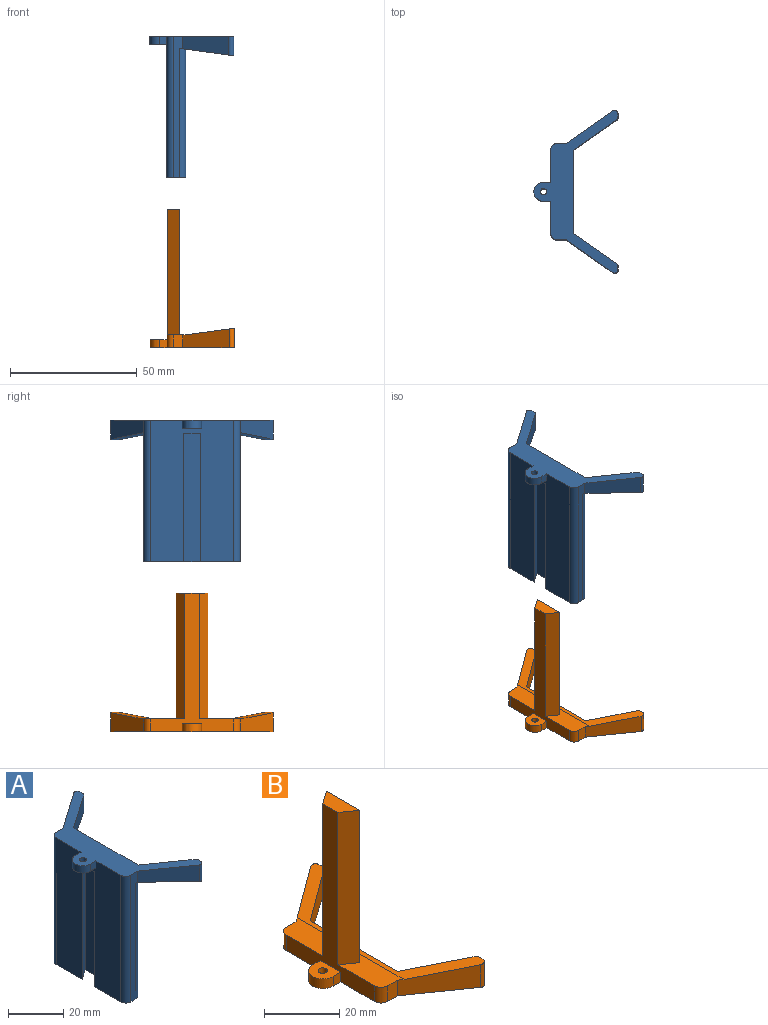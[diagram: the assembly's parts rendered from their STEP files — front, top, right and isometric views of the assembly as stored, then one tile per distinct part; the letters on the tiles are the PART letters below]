
ASSEMBLY  parts=2 mates=1
PART A: 31 faces, bbox 33.1x64.2x55.9 mm
  f0: plane 7.62x1.43mm, normal (1,0,0), area 10.9mm2, adj f4,f6,f28,f29
  f1: plane 55.88x33.02mm, normal (-1,0,0), area 1498.6mm2, adj f2,f6,f9,f11,f12,f13,f15,f17
  f2: plane 38.1x7.62mm, normal (0,0,-1), area 234.3mm2, adj f1,f3,f7,f8,f9,f10,f11,f18
  f3: plane 50.8x33.02mm, normal (1,0,0), area 1677.4mm2, adj f2,f4,f18,f20
  f4: plane 64.23x21.42mm, normal (-0.13,0,-0.99), area 215.4mm2, adj f0,f3,f5,f7,f8,f18,f20,f22
  f5: plane 7.62x1.43mm, normal (1,0,0), area 10.9mm2, adj f4,f6,f27,f30
  f6: plane 64.23x33.14mm, normal (0,0,1), area 537.4mm2, adj f0,f1,f5,f7,f8,f13,f14,f15
  f7: plane 55.88x3.63mm, normal (0,-1,0), area 147.2mm2, adj f2,f4,f6,f20,f21,f23
  f8: plane 55.88x3.63mm, normal (0,1,0), area 147.2mm2, adj f2,f4,f6,f18,f19,f22
  f9: plane 50.8x5.08mm, normal (0.58,-0.82,0), area 316.2mm2, adj f1,f2,f10,f12
  f10: plane 50.8x13.55mm, normal (-1,0,0), area 688.1mm2, adj f2,f9,f11,f12
  f11: plane 50.8x5.08mm, normal (0.58,0.82,0), area 316.2mm2, adj f1,f2,f10,f12
  f12: plane 13.55x5.08mm, normal (0,0,-1), area 50.5mm2, adj f1,f9,f10,f11
  f13: plane 3.18x2.78mm, normal (0.01,1,0), area 8.8mm2, adj f1,f6,f14,f17
  f14: cylinder r=3.81mm len=7.62mm, axis (0,0,1), area 38.3mm2, adj f6,f13,f15,f17
  f15: plane 3.18x2.78mm, normal (0.01,-1,0), area 8.8mm2, adj f1,f6,f14,f17
  f16: cylinder r=1.27mm len=3.18mm, axis (0,0,1), area 25.3mm2, adj f6,f17
  f17: plane 7.62x6.64mm, normal (0,0,-1), area 39.2mm2, adj f1,f13,f14,f15,f16
  f18: cylinder r=2.54mm len=51.14mm, axis (0,0,1), area 203.2mm2, adj f2,f3,f4,f8
  f19: cylinder r=2.54mm len=55.88mm, axis (0,0,-1), area 223mm2, adj f1,f2,f6,f8
  f20: cylinder r=2.54mm len=51.14mm, axis (0,0,-1), area 203.2mm2, adj f2,f3,f4,f7
  f21: cylinder r=2.54mm len=55.88mm, axis (0,0,1), area 223mm2, adj f1,f2,f6,f7
  f22: plane 18.33x12.84mm, normal (-0.57,0.82,0), area 136.9mm2, adj f4,f6,f8,f30
  f23: plane 18.33x12.84mm, normal (-0.57,-0.82,0), area 136.9mm2, adj f4,f6,f7,f29
  f24: plane 17.06x11.95mm, normal (0.57,-0.82,0), area 133.3mm2, adj f4,f6,f25,f27
  f25: plane 32.85x5.25mm, normal (1,0,0), area 172.5mm2, adj f4,f6,f24,f26
  f26: plane 17.06x11.95mm, normal (0.57,0.82,0), area 133.3mm2, adj f4,f6,f25,f28
  f27: cylinder r=1.27mm len=7.62mm, axis (0,0,-1), area 9.3mm2, adj f4,f5,f6,f24
  f28: cylinder r=1.27mm len=7.62mm, axis (0,0,1), area 9.3mm2, adj f0,f4,f6,f26
  f29: cylinder r=1.27mm len=7.62mm, axis (0,0,-1), area 20.8mm2, adj f0,f4,f6,f23
  f30: cylinder r=1.27mm len=7.62mm, axis (0,0,-1), area 20.8mm2, adj f4,f5,f6,f22
PART B: 28 faces, bbox 33.1x64.2x54.6 mm
  f0: plane 7.62x1.43mm, normal (1,0,0), area 10.9mm2, adj f1,f2,f22,f24
  f1: plane 64.23x33.14mm, normal (0,0,-1), area 537.4mm2, adj f0,f3,f8,f9,f11,f12,f13,f14
  f2: plane 64.23x18.88mm, normal (-0.13,0,0.99), area 211.1mm2, adj f0,f10,f11,f17,f18,f19,f20,f21
  f3: plane 54.61x33.02mm, normal (-1,0,0), area 427.5mm2, adj f1,f4,f5,f7,f10,f13,f15,f16
  f4: plane 49.53x4.83mm, normal (-0.58,-0.82,0), area 292.9mm2, adj f3,f6,f7,f10
  f5: plane 49.53x4.83mm, normal (-0.58,0.82,0), area 292.9mm2, adj f3,f6,f7,f10
  f6: plane 49.53x12.56mm, normal (1,0,0), area 622.2mm2, adj f4,f5,f7,f10
  f7: plane 12.56x4.83mm, normal (0,0,1), area 44.1mm2, adj f3,f4,f5,f6
  f8: plane 5.08x3.63mm, normal (0,1,0), area 18.4mm2, adj f1,f10,f18,f26
  f9: plane 5.08x3.63mm, normal (0,-1,0), area 18.4mm2, adj f1,f10,f17,f27
  f10: plane 40.13x7.62mm, normal (0,0,1), area 244.9mm2, adj f2,f3,f4,f5,f6,f8,f9,f17
  f11: plane 7.62x1.43mm, normal (1,0,0), area 10.9mm2, adj f1,f2,f23,f25
  f12: cylinder r=3.81mm len=7.62mm, axis (0,0,-1), area 38.3mm2, adj f1,f13,f15,f16
  f13: plane 3.18x2.78mm, normal (0.01,1,0), area 8.8mm2, adj f1,f3,f12,f16
  f14: cylinder r=1.27mm len=3.18mm, axis (0,0,-1), area 25.3mm2, adj f1,f16
  f15: plane 3.18x2.78mm, normal (0.01,-1,0), area 8.8mm2, adj f1,f3,f12,f16
  f16: plane 7.62x6.64mm, normal (0,0,1), area 39.2mm2, adj f3,f12,f13,f14,f15
  f17: plane 18.33x12.84mm, normal (-0.57,-0.82,0), area 137.1mm2, adj f1,f2,f9,f10,f25
  f18: plane 18.33x12.84mm, normal (-0.57,0.82,0), area 137.1mm2, adj f1,f2,f8,f10,f24
  f19: plane 17.06x11.95mm, normal (0.57,0.82,0), area 133.3mm2, adj f1,f2,f20,f23
  f20: plane 32.85x5.25mm, normal (1,0,0), area 172.5mm2, adj f1,f2,f19,f21
  f21: plane 17.06x11.95mm, normal (0.57,-0.82,0), area 133.3mm2, adj f1,f2,f20,f22
  f22: cylinder r=1.27mm len=7.62mm, axis (0,0,1), area 9.3mm2, adj f0,f1,f2,f21
  f23: cylinder r=1.27mm len=7.62mm, axis (0,0,-1), area 9.3mm2, adj f1,f2,f11,f19
  f24: cylinder r=1.27mm len=7.62mm, axis (0,0,1), area 20.8mm2, adj f0,f1,f2,f18
  f25: cylinder r=1.27mm len=7.62mm, axis (0,0,1), area 20.8mm2, adj f1,f2,f11,f17
  f26: cylinder r=2.54mm len=5.08mm, axis (0,0,-1), area 20.3mm2, adj f1,f3,f8,f10
  f27: cylinder r=2.54mm len=5.08mm, axis (0,0,1), area 20.3mm2, adj f1,f3,f9,f10
PLACE A t=(-11.77,-3.83,-5.12)mm fixed
PLACE B t=(-11.64,-3.83,-67.05)mm
MATE slider B.f7 <-> A.f12  axis (0,0,1) through (-8.93,-22.88,-73.4)mm
